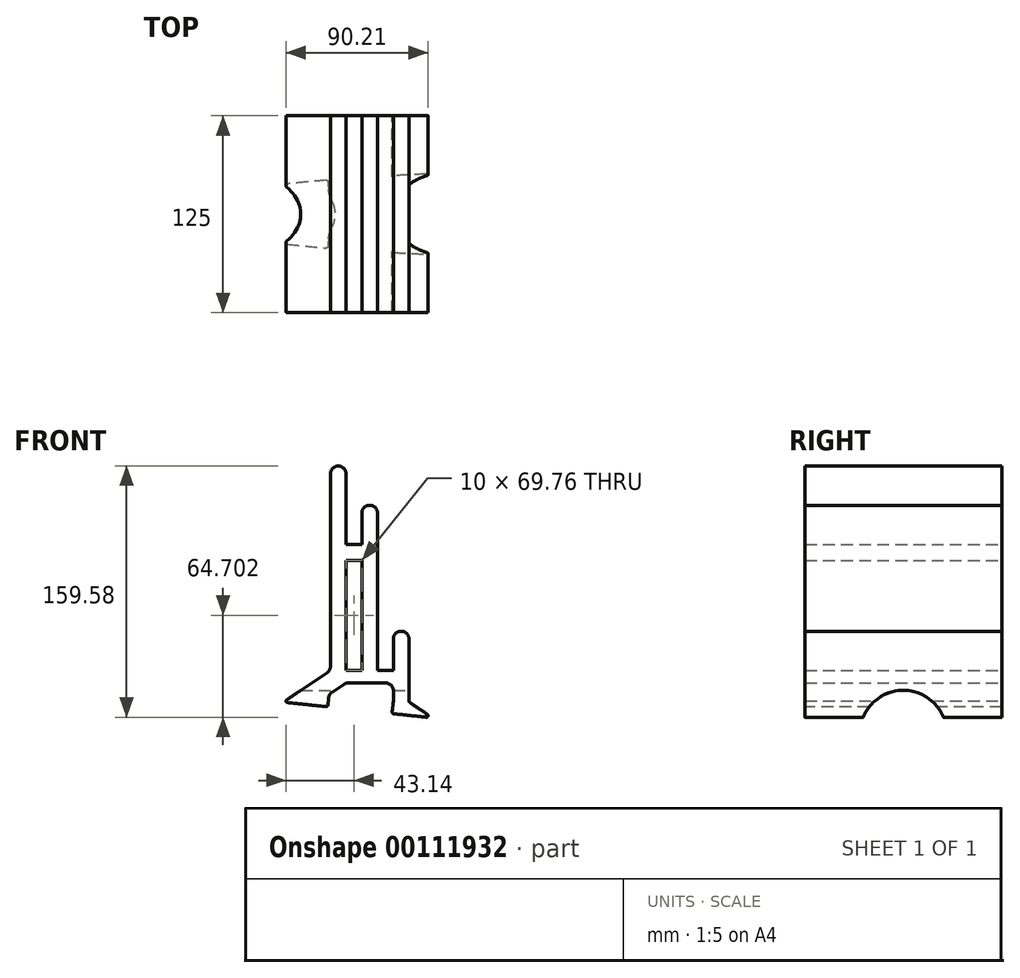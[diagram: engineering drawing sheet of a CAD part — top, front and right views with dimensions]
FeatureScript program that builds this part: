
annotation { "Feature Type Name" : "Feature", "Feature Type Description" : "" }
export const myFeature = defineFeature(function(context is Context, id is Id, definition is map)
    precondition{}
    {
        {
            var Q0;
            Q0=qCreatedBy(makeId("Front.planeOp"),FACE);
            var sketch = newSketch(context, id + "F0", { "sketchPlane" : qUnion([Q0])});
            skLineSegment(sketch, "E0", {"start": v(-50, 20) * mm, "end": v(-50, 150) * mm});
            skLineSegment(sketch, "E1", {"start": v(-50, 150) * mm, "end": v(-40, 150) * mm});
            skLineSegment(sketch, "E2", {"start": v(-40, 150) * mm, "end": v(-40, 100) * mm});
            skLineSegment(sketch, "E3", {"start": v(-40, 100) * mm, "end": v(-30, 100) * mm});
            skLineSegment(sketch, "E4", {"start": v(-30, 100) * mm, "end": v(-30, 125) * mm});
            skLineSegment(sketch, "E5", {"start": v(-30, 125) * mm, "end": v(-20, 125) * mm});
            skLineSegment(sketch, "E6", {"start": v(-20, 125) * mm, "end": v(-20, 20) * mm});
            skLineSegment(sketch, "E7", {"start": v(-20, 20) * mm, "end": v(-10, 20) * mm});
            skLineSegment(sketch, "E8", {"start": v(-10, 20) * mm, "end": v(-10, 45) * mm});
            skLineSegment(sketch, "E9", {"start": v(-10, 45) * mm, "end": v(0, 45) * mm});
            skLineSegment(sketch, "E10", {"start": v(0, 45) * mm, "end": v(0, 0) * mm});
            skLineSegment(sketch, "E11", {"start": v(-50, 20) * mm, "end": v(-80, 0) * mm});
            skLineSegment(sketch, "E12", {"start": v(-80, 0) * mm, "end": v(-51.73, -2.98) * mm});
            skLineSegment(sketch, "E13", {"start": v(15, -10) * mm, "end": v(0, 0) * mm});
            skPoint(sketch, "E14.orphan", {"position": v(-50, 0) * mm});
            skLineSegment(sketch, "E15", {"start": v(-40, 90) * mm, "end": v(-40, 20.24) * mm});
            skLineSegment(sketch, "E16", {"start": v(-40, 12.24) * mm, "end": v(-50.9, 4.98) * mm});
            skLineSegment(sketch, "E17", {"start": v(-50.9, 4.98) * mm, "end": v(-10, 0.68) * mm, "construction": true});
            skLineSegment(sketch, "E18", {"start": v(-10, 0.68) * mm, "end": v(-10, 10) * mm});
            skLineSegment(sketch, "E19", {"start": v(-10, 10) * mm, "end": v(-30, 10) * mm, "construction": true});
            skLineSegment(sketch, "E20", {"start": v(-30, 10) * mm, "end": v(-30, 12.24) * mm, "construction": true});
            skLineSegment(sketch, "E21", {"start": v(-30, 90) * mm, "end": v(-40, 90) * mm});
            skLineSegment(sketch, "E22", {"start": v(-10, 20) * mm, "end": v(-10, 10) * mm, "construction": true});
            skLineSegment(sketch, "E23", {"start": v(-25, 2.25) * mm, "end": v(-25.84, -5.7) * mm, "construction": true});
            skLineSegment(sketch, "E24", {"start": v(-45.45, 8.61) * mm, "end": v(-52.1, 18.6) * mm, "construction": true});
            skLineSegment(sketch, "E25", {"start": v(-50.9, 4.98) * mm, "end": v(-51.73, -2.98) * mm});
            skLineSegment(sketch, "E26", {"start": v(-10, 0.68) * mm, "end": v(-10.84, -7.28) * mm});
            skLineSegment(sketch, "E27.trimOffspring", {"start": v(-10.84, -7.28) * mm, "end": v(15, -10) * mm});
            skLineSegment(sketch, "E28", {"start": v(-40, 12.24) * mm, "end": v(-30, 12.24) * mm});
            skLineSegment(sketch, "E29", {"start": v(-40, 20.24) * mm, "end": v(-30, 20.24) * mm});
            skLineSegment(sketch, "E30.trimOffspring", {"start": v(-30, 20.24) * mm, "end": v(-30, 90) * mm});
            skLineSegment(sketch, "E31", {"start": v(-30, 12.24) * mm, "end": v(-10, 0.68) * mm, "construction": true});
            skLineSegment(sketch, "E32", {"start": v(-30, 12.24) * mm, "end": v(-10, 12.24) * mm});
            skLineSegment(sketch, "E33", {"start": v(-10, 12.24) * mm, "end": v(-10, 10) * mm});
            skSolve(sketch);
        }
        {
            var Q0;
            Q0=makeQuery(id+"F0.imprint","IMPRINT",FACE,{"disambiguationData":[TD([[makeQuery(id+"F0.imprint","IMPRINT",EDGE,{"derivedFrom":sQuery(id+"F0.wireOp",EDGE,"E0")}),-1.0]])]});
            extrude(context, id + "F1", {"entities" : qUnion([Q0]), "depth" : 125 * mm});
        }
        {
            var Q0;
            Q0=makeQuery(id+"F1.opExtrude","SWEPT_EDGE",EDGE,{"disambiguationData":[OSD([sQuery(id+"F0.wireOp",EDGE,"E11"),sQuery(id+"F0.wireOp",EDGE,"E12")])]});
            var Q1;
            Q1=makeQuery(id+"F1.opExtrude","SWEPT_EDGE",EDGE,{"disambiguationData":[OSD([sQuery(id+"F0.wireOp",EDGE,"E12"),sQuery(id+"F0.wireOp",EDGE,"E13")])]});
            fillet(context, id + "F2", {"entities" : qUnion([Q0, Q1]), "radius" : 1 * mm, "tangentPropagation" : true, "allowEdgeOverflow" : false});
        }
        {
            var Q0;
            Q0=makeQuery(id+"F1.opExtrude","SWEPT_EDGE",EDGE,{"disambiguationData":[OSD([sQuery(id+"F0.wireOp",EDGE,"E9"),sQuery(id+"F0.wireOp",EDGE,"E10")])]});
            var Q1;
            Q1=makeQuery(id+"F1.opExtrude","SWEPT_EDGE",EDGE,{"disambiguationData":[OSD([sQuery(id+"F0.wireOp",EDGE,"E8"),sQuery(id+"F0.wireOp",EDGE,"E9")])]});
            var Q2;
            Q2=makeQuery(id+"F1.opExtrude","SWEPT_EDGE",EDGE,{"disambiguationData":[OSD([sQuery(id+"F0.wireOp",EDGE,"E5"),sQuery(id+"F0.wireOp",EDGE,"E6")])]});
            var Q3;
            Q3=makeQuery(id+"F1.opExtrude","SWEPT_EDGE",EDGE,{"disambiguationData":[OSD([sQuery(id+"F0.wireOp",EDGE,"E4"),sQuery(id+"F0.wireOp",EDGE,"E5")])]});
            var Q4;
            Q4=makeQuery(id+"F1.opExtrude","SWEPT_EDGE",EDGE,{"disambiguationData":[OSD([sQuery(id+"F0.wireOp",EDGE,"E1"),sQuery(id+"F0.wireOp",EDGE,"E2")])]});
            var Q5;
            Q5=makeQuery(id+"F1.opExtrude","SWEPT_EDGE",EDGE,{"disambiguationData":[OSD([sQuery(id+"F0.wireOp",EDGE,"E0"),sQuery(id+"F0.wireOp",EDGE,"E1")])]});
            fillet(context, id + "F3", {"entities" : qUnion([Q0, Q1, Q2, Q3, Q4, Q5]), "radius" : 5 * mm, "tangentPropagation" : true, "allowEdgeOverflow" : false});
        }
        {
            var Q0;
            Q0=makeQuery(id+"F1.opExtrude","SWEPT_EDGE",EDGE,{"disambiguationData":[OSD([sQuery(id+"F0.wireOp",EDGE,"E26"),sQuery(id+"F0.wireOp",EDGE,"E27.trimOffspring")])]});
            fillet(context, id + "F4", {"entities" : qUnion([Q0]), "radius" : 1 * mm, "tangentPropagation" : true, "allowEdgeOverflow" : false});
        }
        {
            var Q0;
            Q0=makeQuery(id+"F1.opExtrude","SWEPT_EDGE",EDGE,{"disambiguationData":[OSD([sQuery(id+"F0.wireOp",EDGE,"E16"),sQuery(id+"F0.wireOp",EDGE,"E25")])]});
            var Q1;
            Q1=makeQuery(id+"F1.opExtrude","SWEPT_EDGE",EDGE,{"disambiguationData":[OSD([sQuery(id+"F0.wireOp",EDGE,"E16"),sQuery(id+"F0.wireOp",EDGE,"E28")])]});
            var Q2;
            Q2=makeQuery(id+"F1.opExtrude","SWEPT_EDGE",EDGE,{"disambiguationData":[OSD([sQuery(id+"F0.wireOp",EDGE,"E32"),sQuery(id+"F0.wireOp",EDGE,"E33")])]});
            fillet(context, id + "F5", {"entities" : qUnion([Q0, Q1, Q2]), "radius" : 5 * mm, "tangentPropagation" : true, "allowEdgeOverflow" : false});
        }
        {
            var Q0;
            Q0=makeQuery(id+"F1.opExtrude","SWEPT_EDGE",EDGE,{"disambiguationData":[OSD([sQuery(id+"F0.wireOp",EDGE,"E0"),sQuery(id+"F0.wireOp",EDGE,"E11")])]});
            fillet(context, id + "F6", {"entities" : qUnion([Q0]), "radius" : 5 * mm, "tangentPropagation" : true, "allowEdgeOverflow" : false});
        }
        {
            var Q0;
            Q0=qCreatedBy(makeId("Right.planeOp"),FACE);
            cPlane(context, id + "F7", {"entities" : qUnion([Q0]), "cplaneType" : CPlaneType.OFFSET, "offset" : 50 * mm, "width" : 150 * mm, "height" : 150 * mm});
        }
        {
            var Q0;
            Q0=qCreatedBy(id+"F7.planeOp",FACE);
            var sketch = newSketch(context, id + "F8", { "sketchPlane" : qUnion([Q0])});
            skLineSegment(sketch, "E34.0", {"start": v(-125, -7.75) * mm, "end": v(0, -7.75) * mm, "construction": true});
            skLineSegment(sketch, "E35", {"start": v(0, -20) * mm, "end": v(-125, -20) * mm, "construction": true});
            skCircle(sketch, "E36", {"center": v(-62.5, -20) * mm, "radius": 27.5 * mm});
            skSolve(sketch);
        }
        {
            var Q0;
            Q0 = qSketchRegion(id + "F8", true);
            extrude(context, id + "F9", {"entities" : qUnion([Q0]), "operationType" : NewBodyOperationType.REMOVE, "endBound" : BoundingType.THROUGH_ALL, "oppositeDirection" : true, "depth" : 25 * mm});
        }
    });
